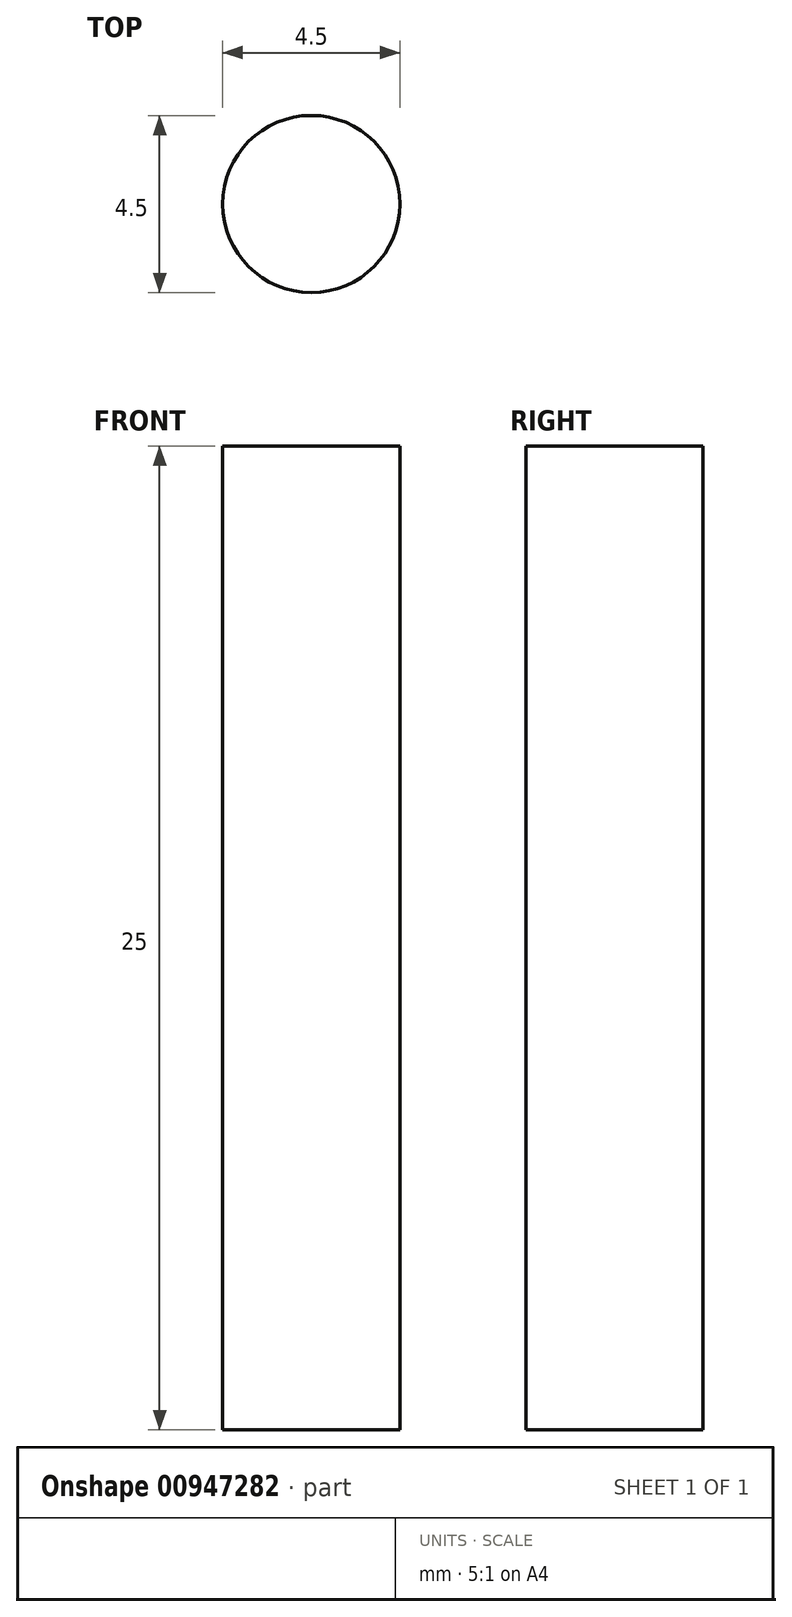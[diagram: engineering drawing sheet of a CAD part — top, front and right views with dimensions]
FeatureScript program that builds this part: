
annotation { "Feature Type Name" : "Feature", "Feature Type Description" : "" }
export const myFeature = defineFeature(function(context is Context, id is Id, definition is map)
    precondition{}
    {
        {
            var Q0;
            Q0=qCreatedBy(makeId("Top.planeOp"),FACE);
            var sketch = newSketch(context, id + "F0", { "sketchPlane" : qUnion([Q0])});
            skCircle(sketch, "E0", {"center": v(0, 0) * mm, "radius": 2.25 * mm});
            skSolve(sketch);
        }
        {
            var Q0;
            Q0 = qSketchRegion(id + "F0", true);
            extrude(context, id + "F1", {"entities" : qUnion([Q0]), "endBound" : BoundingType.SYMMETRIC, "depth" : 25 * mm, "offsetDistance" : 25 * mm});
        }
    });
